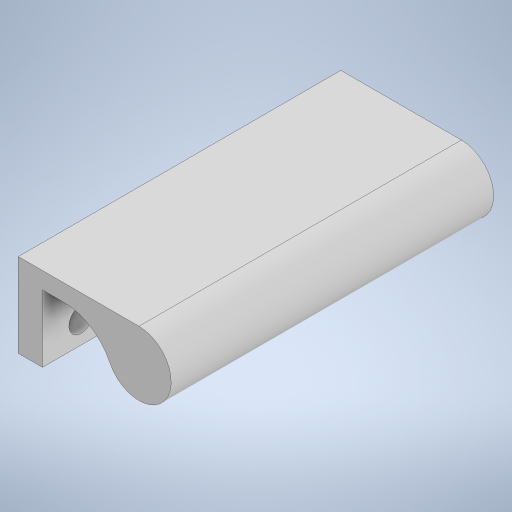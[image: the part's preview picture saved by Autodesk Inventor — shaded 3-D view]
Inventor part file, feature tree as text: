
AUTODESK INVENTOR PART (.ipt)
format: ipt  version: 2024.2 (Build 282272000, 272)  size: 263,680 bytes
history: native  units: in
note: dims shown in document units (in); Inventor stores cm internally (conversion verified against a paired STEP export)
features: extrude x3, sketch x3
ambient origin geometry x8: Origin, YZ Plane, XZ Plane, XY Plane, X Axis, Y Axis, Z Axis, Center Point
bodies: Solid1 (feature_tree)
feature tree (6):
  extrude  "Extrusion1"  Depth=0.65in
  extrude  "Extrusion2"  Depth=0.3937in
  extrude  "Extrusion3"  Depth=0.13in
  sketch  "Sketch1"  dims[d0=2.5in d1=0.65in]
  sketch  "Sketch2"  dims[d4=2.7559in d6=0.3149in d7=0.3937in d9=1.0in d11=0.3in]
  sketch  "Sketch3"  dims[d12=0.1875in d13=0.0in d14=0.13in d15=0.04in d16=0.0in d17=0.935in d18=0.5in d20=2.5in d21=0.0in]
